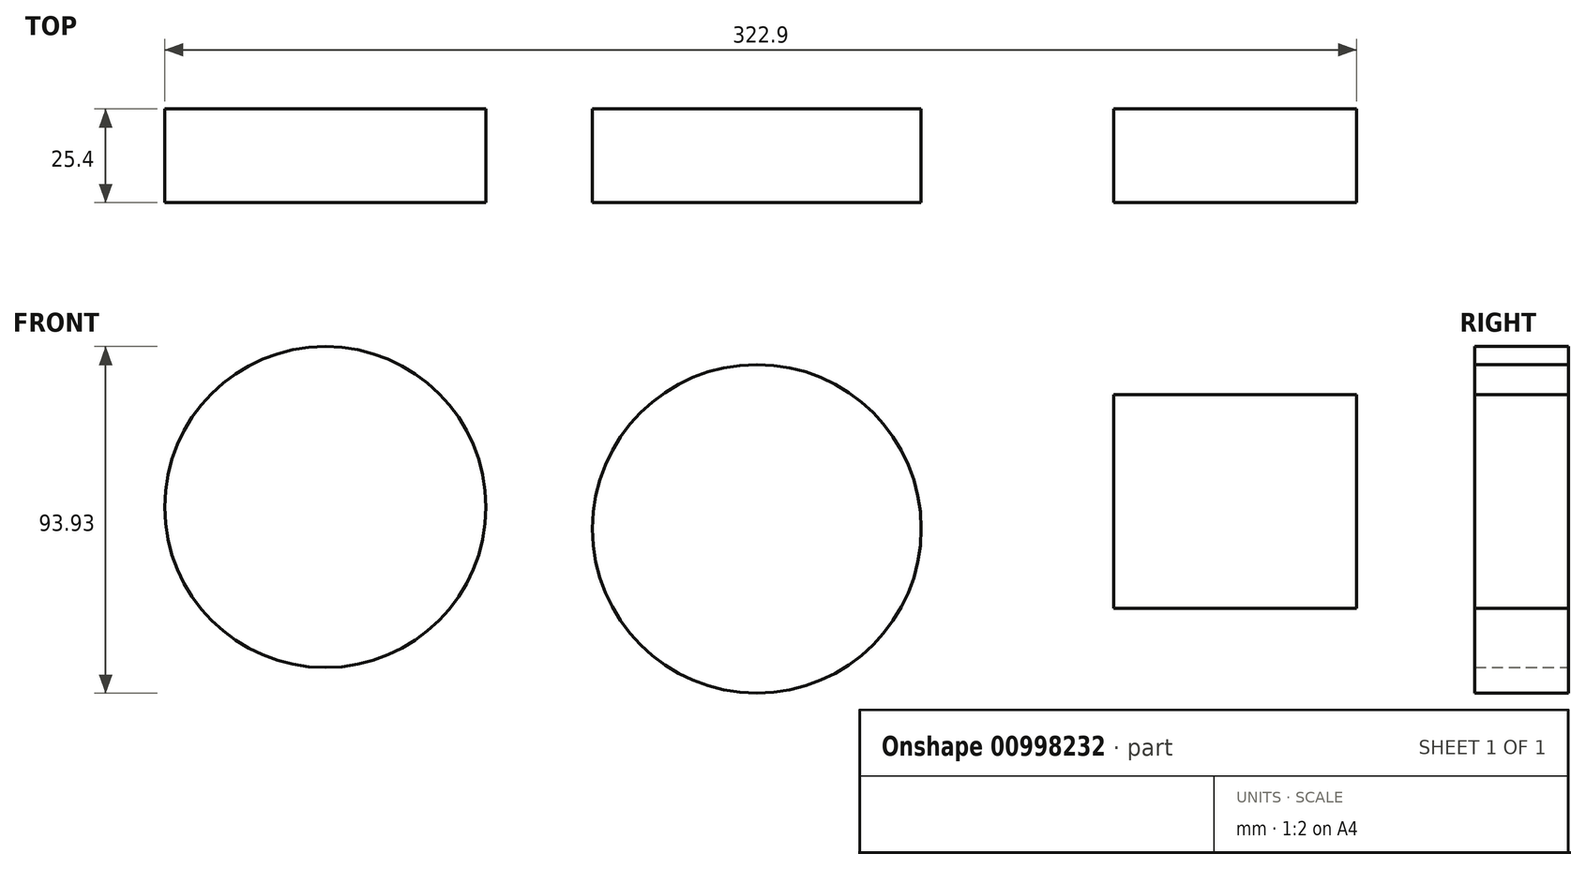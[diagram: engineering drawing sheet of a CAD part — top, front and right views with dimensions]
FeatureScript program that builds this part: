
annotation { "Feature Type Name" : "Feature", "Feature Type Description" : "" }
export const myFeature = defineFeature(function(context is Context, id is Id, definition is map)
    precondition{}
    {
        {
            var Q0;
            Q0=qCreatedBy(makeId("Front.planeOp"),FACE);
            var sketch = newSketch(context, id + "F0", { "sketchPlane" : qUnion([Q0])});
            skCircle(sketch, "E0", {"center": v(-43.25, 66.55) * mm, "radius": 43.5 * mm});
            skCircle(sketch, "E1", {"center": v(73.63, 60.64) * mm, "radius": 44.52 * mm});
            skSolve(sketch);
        }
        {
            var Q0;
            Q0 = qSketchRegion(id + "F0", true);
            extrude(context, id + "F1", {"entities" : qUnion([Q0]), "depth" : 25.4 * mm, "offsetDistance" : 25.4 * mm});
        }
        {
            var Q0;
            Q0=qCreatedBy(makeId("Front.planeOp"),FACE);
            var sketch = newSketch(context, id + "F2", { "sketchPlane" : qUnion([Q0])});
            skLineSegment(sketch, "E2.bottom", {"start": v(236.15, 39.13) * mm, "end": v(170.34, 39.13) * mm});
            skLineSegment(sketch, "E2.top", {"start": v(236.15, 97.03) * mm, "end": v(170.34, 97.03) * mm});
            skLineSegment(sketch, "E2.left", {"start": v(236.15, 39.13) * mm, "end": v(236.15, 97.03) * mm});
            skLineSegment(sketch, "E2.right", {"start": v(170.34, 39.13) * mm, "end": v(170.34, 97.03) * mm});
            skPoint(sketch, "E2.middle", {"position": v(203.24, 68.08) * mm});
            skArc(sketch, "E3", {"start": v(215.1, 245.23) * mm, "mid": v(269.84, 242.88) * mm, "end": v(320.07, 220.98) * mm});
            skSolve(sketch);
        }
        {
            var Q0;
            Q0=makeQuery(id+"F2.imprint","IMPRINT",FACE,{"disambiguationData":[TD([[makeQuery(id+"F2.imprint","IMPRINT",EDGE,{"derivedFrom":sQuery(id+"F2.wireOp",EDGE,"E2.bottom")}),-1.0]])]});
            extrude(context, id + "F3", {"entities" : qUnion([Q0]), "depth" : 25.4 * mm, "offsetDistance" : 25.4 * mm});
        }
    });
